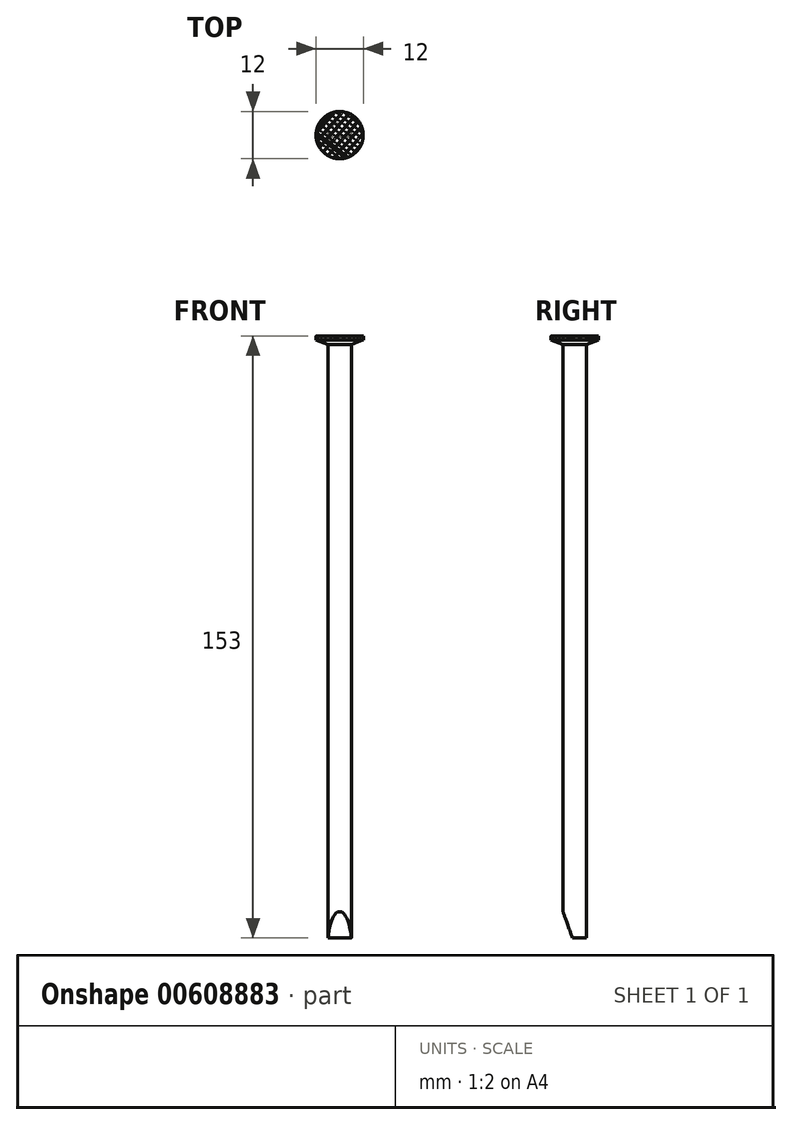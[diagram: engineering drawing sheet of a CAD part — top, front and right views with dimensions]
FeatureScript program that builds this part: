
annotation { "Feature Type Name" : "Feature", "Feature Type Description" : "" }
export const myFeature = defineFeature(function(context is Context, id is Id, definition is map)
    precondition{}
    {
        {
            var Q0;
            Q0=qCreatedBy(makeId("Top.planeOp"),FACE);
            var sketch = newSketch(context, id + "F0", { "sketchPlane" : qUnion([Q0])});
            skCircle(sketch, "E0", {"center": v(0, 0) * mm, "radius": 3 * mm});
            skSolve(sketch);
        }
        {
            var Q0;
            Q0=makeQuery(id+"F0.imprint","IMPRINT",FACE,{"disambiguationData":[TD([[makeQuery(id+"F0.imprint","IMPRINT",EDGE,{"derivedFrom":sQuery(id+"F0.wireOp",EDGE,"E0")}),1.0]])]});
            extrude(context, id + "F1", {"entities" : qUnion([Q0]), "depth" : 150 * mm, "offsetDistance" : 25 * mm});
        }
        {
            var Q0;
            Q0=makeQuery(id+"F1.opExtrude","CAP_FACE",FACE,{"disambiguationData":[OSD([sQuery(id+"F0.wireOp",EDGE,"E0")])],"isStart":false});
            var sketch = newSketch(context, id + "F2", { "sketchPlane" : qUnion([Q0])});
            skCircle(sketch, "E1", {"center": v(0, 0) * mm, "radius": 6 * mm});
            skSolve(sketch);
        }
        {
            var Q0;
            Q0 = qSketchRegion(id + "F2", true);
            extrude(context, id + "F3", {"entities" : qUnion([Q0]), "operationType" : NewBodyOperationType.ADD, "depth" : 3 * mm, "offsetDistance" : 25 * mm});
        }
        {
            var Q0;
            Q0=makeQuery(id+"F3.opExtrude","CAP_EDGE",EDGE,{"disambiguationData":[OSD([sQuery(id+"F2.wireOp",EDGE,"E1")])],"isStart":true});
            chamfer(context, id + "F4", {"entities" : qUnion([Q0]), "chamferType" : ChamferType.TWO_OFFSETS, "width1" : 2 * mm, "oppositeDirection" : false, "width2" : 5 * mm, "tangentPropagation" : true});
        }
        {
            var Q0;
            Q0=makeQuery(id+"F3.opExtrude","CAP_FACE",FACE,{"disambiguationData":[OSD([sQuery(id+"F2.wireOp",EDGE,"E1")])],"isStart":false});
            var sketch = newSketch(context, id + "F5", { "sketchPlane" : qUnion([Q0])});
            skLineSegment(sketch, "E2", {"start": v(-21.1, 10.28) * mm, "end": v(9.5, -13.54) * mm});
            skLineSegment(sketch, "E3", {"start": v(9.5, -13.54) * mm, "end": v(9.07, -14.09) * mm});
            skLineSegment(sketch, "E4", {"start": v(9.07, -14.09) * mm, "end": v(-21.1, 9.4) * mm});
            skLineSegment(sketch, "E5", {"start": v(-21.1, 9.4) * mm, "end": v(-21.1, 10.28) * mm});
            skLineSegment(sketch, "E6.1.0.0", {"start": v(-19.1, 10.28) * mm, "end": v(11.5, -13.54) * mm});
            skLineSegment(sketch, "E6.1.0.1", {"start": v(11.07, -14.09) * mm, "end": v(-19.1, 9.4) * mm});
            skLineSegment(sketch, "E6.1.0.2", {"start": v(-19.1, 9.4) * mm, "end": v(-19.1, 10.28) * mm});
            skLineSegment(sketch, "E6.1.0.3", {"start": v(11.5, -13.54) * mm, "end": v(11.07, -14.09) * mm});
            skLineSegment(sketch, "E6.2.0.0", {"start": v(-17.1, 10.28) * mm, "end": v(13.5, -13.54) * mm});
            skLineSegment(sketch, "E6.2.0.1", {"start": v(13.07, -14.09) * mm, "end": v(-17.1, 9.4) * mm});
            skLineSegment(sketch, "E6.2.0.2", {"start": v(-17.1, 9.4) * mm, "end": v(-17.1, 10.28) * mm});
            skLineSegment(sketch, "E6.2.0.3", {"start": v(13.5, -13.54) * mm, "end": v(13.07, -14.09) * mm});
            skLineSegment(sketch, "E6.3.0.0", {"start": v(-15.1, 10.28) * mm, "end": v(15.5, -13.54) * mm});
            skLineSegment(sketch, "E6.3.0.1", {"start": v(15.07, -14.09) * mm, "end": v(-15.1, 9.4) * mm});
            skLineSegment(sketch, "E6.3.0.2", {"start": v(-15.1, 9.4) * mm, "end": v(-15.1, 10.28) * mm});
            skLineSegment(sketch, "E6.3.0.3", {"start": v(15.5, -13.54) * mm, "end": v(15.07, -14.09) * mm});
            skLineSegment(sketch, "E6.4.0.0", {"start": v(-13.1, 10.28) * mm, "end": v(17.5, -13.54) * mm});
            skLineSegment(sketch, "E6.4.0.1", {"start": v(17.07, -14.09) * mm, "end": v(-13.1, 9.4) * mm});
            skLineSegment(sketch, "E6.4.0.2", {"start": v(-13.1, 9.4) * mm, "end": v(-13.1, 10.28) * mm});
            skLineSegment(sketch, "E6.4.0.3", {"start": v(17.5, -13.54) * mm, "end": v(17.07, -14.09) * mm});
            skLineSegment(sketch, "E6.5.0.0", {"start": v(-11.1, 10.28) * mm, "end": v(19.5, -13.54) * mm});
            skLineSegment(sketch, "E6.5.0.1", {"start": v(19.07, -14.09) * mm, "end": v(-11.1, 9.4) * mm});
            skLineSegment(sketch, "E6.5.0.2", {"start": v(-11.1, 9.4) * mm, "end": v(-11.1, 10.28) * mm});
            skLineSegment(sketch, "E6.5.0.3", {"start": v(19.5, -13.54) * mm, "end": v(19.07, -14.09) * mm});
            skLineSegment(sketch, "E6.6.0.0", {"start": v(-9.1, 10.28) * mm, "end": v(21.5, -13.54) * mm});
            skLineSegment(sketch, "E6.6.0.1", {"start": v(21.07, -14.09) * mm, "end": v(-9.1, 9.4) * mm});
            skLineSegment(sketch, "E6.6.0.2", {"start": v(-9.1, 9.4) * mm, "end": v(-9.1, 10.28) * mm});
            skLineSegment(sketch, "E6.6.0.3", {"start": v(21.5, -13.54) * mm, "end": v(21.07, -14.09) * mm});
            skLineSegment(sketch, "E6.7.0.0", {"start": v(-7.1, 10.28) * mm, "end": v(23.5, -13.54) * mm});
            skLineSegment(sketch, "E6.7.0.1", {"start": v(23.07, -14.09) * mm, "end": v(-7.1, 9.4) * mm});
            skLineSegment(sketch, "E6.7.0.2", {"start": v(-7.1, 9.4) * mm, "end": v(-7.1, 10.28) * mm});
            skLineSegment(sketch, "E6.7.0.3", {"start": v(23.5, -13.54) * mm, "end": v(23.07, -14.09) * mm});
            skLineSegment(sketch, "E6.8.0.0", {"start": v(-5.1, 10.28) * mm, "end": v(25.5, -13.54) * mm});
            skLineSegment(sketch, "E6.8.0.1", {"start": v(25.07, -14.09) * mm, "end": v(-5.1, 9.4) * mm});
            skLineSegment(sketch, "E6.8.0.2", {"start": v(-5.1, 9.4) * mm, "end": v(-5.1, 10.28) * mm});
            skLineSegment(sketch, "E6.8.0.3", {"start": v(25.5, -13.54) * mm, "end": v(25.07, -14.09) * mm});
            skLineSegment(sketch, "E6.9.0.0", {"start": v(-3.1, 10.28) * mm, "end": v(27.5, -13.54) * mm});
            skLineSegment(sketch, "E6.9.0.1", {"start": v(27.07, -14.09) * mm, "end": v(-3.1, 9.4) * mm});
            skLineSegment(sketch, "E6.9.0.2", {"start": v(-3.1, 9.4) * mm, "end": v(-3.1, 10.28) * mm});
            skLineSegment(sketch, "E6.9.0.3", {"start": v(27.5, -13.54) * mm, "end": v(27.07, -14.09) * mm});
            skLineSegment(sketch, "E6.direction1", {"start": v(-21.1, 9.4) * mm, "end": v(-19.1, 9.4) * mm, "construction": true});
            skSolve(sketch);
        }
        {
            var Q0;
            {var subQ0=sQuery(id+"F5.wireOp",EDGE,"E5");Q0=makeQuery(id+"F5.imprint","IMPRINT",FACE,{"disambiguationData":[TD([[makeQuery(id+"F5.imprint","IMPRINT",EDGE,{"derivedFrom":subQ0}),-1.0]])]});}
            var Q1;
            {var subQ0=sQuery(id+"F5.wireOp",EDGE,"E6.9.0.1");var subQ1=makeQuery(id+"F3.opExtrude","CAP_EDGE",EDGE,{"disambiguationData":[OSD([sQuery(id+"F2.wireOp",EDGE,"E1")])],"isStart":false});var subQ2=makeQuery(id+"F5.imprint","INTERSECT",VERTEX,{"disambiguationData":[OD(0.0)],"derivedFrom":[subQ1,subQ0]});Q1=makeQuery(id+"F5.imprint","IMPRINT",FACE,{"disambiguationData":[TD([[makeQuery(id+"F5.imprint","IMPRINT",EDGE,{"disambiguationData":[TD([[subQ2,-1.0]])],"derivedFrom":subQ0}),-1.0]])]});}
            var Q2;
            {var subQ0=sQuery(id+"F5.wireOp",EDGE,"E6.8.0.0");var subQ1=makeQuery(id+"F3.opExtrude","CAP_EDGE",EDGE,{"disambiguationData":[OSD([sQuery(id+"F2.wireOp",EDGE,"E1")])],"isStart":false});var subQ2=makeQuery(id+"F5.imprint","INTERSECT",VERTEX,{"disambiguationData":[OD(0.0)],"derivedFrom":[subQ1,subQ0]});Q2=makeQuery(id+"F5.imprint","IMPRINT",FACE,{"disambiguationData":[TD([[makeQuery(id+"F5.imprint","IMPRINT",EDGE,{"disambiguationData":[TD([[subQ2,-1.0]])],"derivedFrom":subQ0}),-1.0]])]});}
            var Q3;
            {var subQ0=sQuery(id+"F5.wireOp",EDGE,"E6.7.0.0");var subQ1=makeQuery(id+"F3.opExtrude","CAP_EDGE",EDGE,{"disambiguationData":[OSD([sQuery(id+"F2.wireOp",EDGE,"E1")])],"isStart":false});var subQ2=makeQuery(id+"F5.imprint","INTERSECT",VERTEX,{"disambiguationData":[OD(0.0)],"derivedFrom":[subQ1,subQ0]});Q3=makeQuery(id+"F5.imprint","IMPRINT",FACE,{"disambiguationData":[TD([[makeQuery(id+"F5.imprint","IMPRINT",EDGE,{"disambiguationData":[TD([[subQ2,-1.0]])],"derivedFrom":subQ0}),-1.0]])]});}
            var Q4;
            {var subQ0=sQuery(id+"F5.wireOp",EDGE,"E6.6.0.0");var subQ1=makeQuery(id+"F3.opExtrude","CAP_EDGE",EDGE,{"disambiguationData":[OSD([sQuery(id+"F2.wireOp",EDGE,"E1")])],"isStart":false});var subQ2=makeQuery(id+"F5.imprint","INTERSECT",VERTEX,{"disambiguationData":[OD(0.0)],"derivedFrom":[subQ1,subQ0]});Q4=makeQuery(id+"F5.imprint","IMPRINT",FACE,{"disambiguationData":[TD([[makeQuery(id+"F5.imprint","IMPRINT",EDGE,{"disambiguationData":[TD([[subQ2,-1.0]])],"derivedFrom":subQ0}),-1.0]])]});}
            var Q5;
            {var subQ0=sQuery(id+"F5.wireOp",EDGE,"E6.5.0.0");var subQ1=makeQuery(id+"F3.opExtrude","CAP_EDGE",EDGE,{"disambiguationData":[OSD([sQuery(id+"F2.wireOp",EDGE,"E1")])],"isStart":false});var subQ2=makeQuery(id+"F5.imprint","INTERSECT",VERTEX,{"disambiguationData":[OD(0.0)],"derivedFrom":[subQ1,subQ0]});Q5=makeQuery(id+"F5.imprint","IMPRINT",FACE,{"disambiguationData":[TD([[makeQuery(id+"F5.imprint","IMPRINT",EDGE,{"disambiguationData":[TD([[subQ2,-1.0]])],"derivedFrom":subQ0}),-1.0]])]});}
            var Q6;
            {var subQ0=sQuery(id+"F5.wireOp",EDGE,"E6.4.0.0");var subQ1=makeQuery(id+"F3.opExtrude","CAP_EDGE",EDGE,{"disambiguationData":[OSD([sQuery(id+"F2.wireOp",EDGE,"E1")])],"isStart":false});var subQ2=makeQuery(id+"F5.imprint","INTERSECT",VERTEX,{"disambiguationData":[OD(0.0)],"derivedFrom":[subQ1,subQ0]});Q6=makeQuery(id+"F5.imprint","IMPRINT",FACE,{"disambiguationData":[TD([[makeQuery(id+"F5.imprint","IMPRINT",EDGE,{"disambiguationData":[TD([[subQ2,-1.0]])],"derivedFrom":subQ0}),-1.0]])]});}
            var Q7;
            {var subQ0=sQuery(id+"F5.wireOp",EDGE,"E6.3.0.0");var subQ1=makeQuery(id+"F3.opExtrude","CAP_EDGE",EDGE,{"disambiguationData":[OSD([sQuery(id+"F2.wireOp",EDGE,"E1")])],"isStart":false});var subQ2=makeQuery(id+"F5.imprint","INTERSECT",VERTEX,{"disambiguationData":[OD(0.0)],"derivedFrom":[subQ1,subQ0]});Q7=makeQuery(id+"F5.imprint","IMPRINT",FACE,{"disambiguationData":[TD([[makeQuery(id+"F5.imprint","IMPRINT",EDGE,{"disambiguationData":[TD([[subQ2,-1.0]])],"derivedFrom":subQ0}),-1.0]])]});}
            var Q8;
            {var subQ0=sQuery(id+"F5.wireOp",EDGE,"E6.2.0.0");var subQ1=makeQuery(id+"F3.opExtrude","CAP_EDGE",EDGE,{"disambiguationData":[OSD([sQuery(id+"F2.wireOp",EDGE,"E1")])],"isStart":false});var subQ2=makeQuery(id+"F5.imprint","INTERSECT",VERTEX,{"disambiguationData":[OD(0.0)],"derivedFrom":[subQ1,subQ0]});Q8=makeQuery(id+"F5.imprint","IMPRINT",FACE,{"disambiguationData":[TD([[makeQuery(id+"F5.imprint","IMPRINT",EDGE,{"disambiguationData":[TD([[subQ2,-1.0]])],"derivedFrom":subQ0}),-1.0]])]});}
            var Q9;
            {var subQ0=sQuery(id+"F5.wireOp",EDGE,"E6.1.0.0");var subQ1=makeQuery(id+"F3.opExtrude","CAP_EDGE",EDGE,{"disambiguationData":[OSD([sQuery(id+"F2.wireOp",EDGE,"E1")])],"isStart":false});var subQ2=makeQuery(id+"F5.imprint","INTERSECT",VERTEX,{"disambiguationData":[OD(0.0)],"derivedFrom":[subQ1,subQ0]});Q9=makeQuery(id+"F5.imprint","IMPRINT",FACE,{"disambiguationData":[TD([[makeQuery(id+"F5.imprint","IMPRINT",EDGE,{"disambiguationData":[TD([[subQ2,-1.0]])],"derivedFrom":subQ0}),-1.0]])]});}
            var Q10;
            {var subQ0=sQuery(id+"F5.wireOp",EDGE,"E2");var subQ1=makeQuery(id+"F3.opExtrude","CAP_EDGE",EDGE,{"disambiguationData":[OSD([sQuery(id+"F2.wireOp",EDGE,"E1")])],"isStart":false});var subQ2=makeQuery(id+"F5.imprint","INTERSECT",VERTEX,{"disambiguationData":[OD(0.0)],"derivedFrom":[subQ1,subQ0]});Q10=makeQuery(id+"F5.imprint","IMPRINT",FACE,{"disambiguationData":[TD([[makeQuery(id+"F5.imprint","IMPRINT",EDGE,{"disambiguationData":[TD([[subQ2,-1.0]])],"derivedFrom":subQ0}),-1.0]])]});}
            extrude(context, id + "F6", {"entities" : qUnion([Q0, Q1, Q2, Q3, Q4, Q5, Q6, Q7, Q8, Q9, Q10]), "operationType" : NewBodyOperationType.REMOVE, "oppositeDirection" : true, "depth" : 0.3 * mm, "offsetDistance" : 25 * mm});
        }
        {
            var Q0;
            {var subQ0=sQuery(id+"F2.wireOp",EDGE,"E1");Q0=makeQuery(id+"F6.boolean.opBoolean","SPLIT",FACE,{"disambiguationData":[TD([makeQuery(id+"F6.opExtrude","SWEPT_FACE",FACE,{"disambiguationData":[OSD([sQuery(id+"F5.wireOp",EDGE,"E6.1.0.0")])]})])],"derivedFrom":makeQuery(id+"F3.opExtrude","CAP_FACE",FACE,{"disambiguationData":[OSD([subQ0])],"isStart":false})});}
            var sketch = newSketch(context, id + "F7", { "sketchPlane" : qUnion([Q0])});
            skLineSegment(sketch, "E7", {"start": v(5.94, 12.42) * mm, "end": v(-14.13, -10.44) * mm});
            skLineSegment(sketch, "E8", {"start": v(-14.13, -10.44) * mm, "end": v(-14.64, -10) * mm});
            skLineSegment(sketch, "E9", {"start": v(-14.64, -10) * mm, "end": v(5.33, 12.76) * mm});
            skLineSegment(sketch, "E10", {"start": v(5.33, 12.76) * mm, "end": v(5.94, 12.42) * mm});
            skLineSegment(sketch, "E11.1.0.0", {"start": v(7.94, 12.42) * mm, "end": v(-12.13, -10.44) * mm});
            skLineSegment(sketch, "E11.1.0.1", {"start": v(-12.64, -10) * mm, "end": v(7.33, 12.76) * mm});
            skLineSegment(sketch, "E11.1.0.2", {"start": v(-12.13, -10.44) * mm, "end": v(-12.64, -10) * mm});
            skLineSegment(sketch, "E11.1.0.3", {"start": v(7.33, 12.76) * mm, "end": v(7.94, 12.42) * mm});
            skLineSegment(sketch, "E11.2.0.0", {"start": v(9.94, 12.42) * mm, "end": v(-10.13, -10.44) * mm});
            skLineSegment(sketch, "E11.2.0.1", {"start": v(-10.64, -10) * mm, "end": v(9.33, 12.76) * mm});
            skLineSegment(sketch, "E11.2.0.2", {"start": v(-10.13, -10.44) * mm, "end": v(-10.64, -10) * mm});
            skLineSegment(sketch, "E11.2.0.3", {"start": v(9.33, 12.76) * mm, "end": v(9.94, 12.42) * mm});
            skLineSegment(sketch, "E11.3.0.0", {"start": v(11.94, 12.42) * mm, "end": v(-8.13, -10.44) * mm});
            skLineSegment(sketch, "E11.3.0.1", {"start": v(-8.64, -10) * mm, "end": v(11.33, 12.76) * mm});
            skLineSegment(sketch, "E11.3.0.2", {"start": v(-8.13, -10.44) * mm, "end": v(-8.64, -10) * mm});
            skLineSegment(sketch, "E11.3.0.3", {"start": v(11.33, 12.76) * mm, "end": v(11.94, 12.42) * mm});
            skLineSegment(sketch, "E11.4.0.0", {"start": v(13.94, 12.42) * mm, "end": v(-6.13, -10.44) * mm});
            skLineSegment(sketch, "E11.4.0.1", {"start": v(-6.64, -10) * mm, "end": v(13.33, 12.76) * mm});
            skLineSegment(sketch, "E11.4.0.2", {"start": v(-6.13, -10.44) * mm, "end": v(-6.64, -10) * mm});
            skLineSegment(sketch, "E11.4.0.3", {"start": v(13.33, 12.76) * mm, "end": v(13.94, 12.42) * mm});
            skLineSegment(sketch, "E11.5.0.0", {"start": v(15.94, 12.42) * mm, "end": v(-4.13, -10.44) * mm});
            skLineSegment(sketch, "E11.5.0.1", {"start": v(-4.64, -10) * mm, "end": v(15.33, 12.76) * mm});
            skLineSegment(sketch, "E11.5.0.2", {"start": v(-4.13, -10.44) * mm, "end": v(-4.64, -10) * mm});
            skLineSegment(sketch, "E11.5.0.3", {"start": v(15.33, 12.76) * mm, "end": v(15.94, 12.42) * mm});
            skLineSegment(sketch, "E11.6.0.0", {"start": v(17.94, 12.42) * mm, "end": v(-2.13, -10.44) * mm});
            skLineSegment(sketch, "E11.6.0.1", {"start": v(-2.64, -10) * mm, "end": v(17.33, 12.76) * mm});
            skLineSegment(sketch, "E11.6.0.2", {"start": v(-2.13, -10.44) * mm, "end": v(-2.64, -10) * mm});
            skLineSegment(sketch, "E11.6.0.3", {"start": v(17.33, 12.76) * mm, "end": v(17.94, 12.42) * mm});
            skLineSegment(sketch, "E11.7.0.0", {"start": v(19.94, 12.42) * mm, "end": v(-0.13, -10.44) * mm});
            skLineSegment(sketch, "E11.7.0.1", {"start": v(-0.64, -10) * mm, "end": v(19.33, 12.76) * mm});
            skLineSegment(sketch, "E11.7.0.2", {"start": v(-0.13, -10.44) * mm, "end": v(-0.64, -10) * mm});
            skLineSegment(sketch, "E11.7.0.3", {"start": v(19.33, 12.76) * mm, "end": v(19.94, 12.42) * mm});
            skLineSegment(sketch, "E11.8.0.0", {"start": v(21.94, 12.42) * mm, "end": v(1.87, -10.44) * mm});
            skLineSegment(sketch, "E11.8.0.1", {"start": v(1.36, -10) * mm, "end": v(21.33, 12.76) * mm});
            skLineSegment(sketch, "E11.8.0.2", {"start": v(1.87, -10.44) * mm, "end": v(1.36, -10) * mm});
            skLineSegment(sketch, "E11.8.0.3", {"start": v(21.33, 12.76) * mm, "end": v(21.94, 12.42) * mm});
            skLineSegment(sketch, "E11.9.0.0", {"start": v(23.94, 12.42) * mm, "end": v(3.87, -10.44) * mm});
            skLineSegment(sketch, "E11.9.0.1", {"start": v(3.36, -10) * mm, "end": v(23.33, 12.76) * mm});
            skLineSegment(sketch, "E11.9.0.2", {"start": v(3.87, -10.44) * mm, "end": v(3.36, -10) * mm});
            skLineSegment(sketch, "E11.9.0.3", {"start": v(23.33, 12.76) * mm, "end": v(23.94, 12.42) * mm});
            skLineSegment(sketch, "E11.direction1", {"start": v(-14.64, -10) * mm, "end": v(-12.64, -10) * mm, "construction": true});
            skSolve(sketch);
        }
        {
            var Q0;
            {var subQ0=sQuery(id+"F7.wireOp",EDGE,"E10");Q0=makeQuery(id+"F7.imprint","IMPRINT",FACE,{"disambiguationData":[TD([[makeQuery(id+"F7.imprint","IMPRINT",EDGE,{"derivedFrom":subQ0}),-1.0]])]});}
            var Q1;
            {var subQ0=sQuery(id+"F7.wireOp",EDGE,"E11.1.0.3");Q1=makeQuery(id+"F7.imprint","IMPRINT",FACE,{"disambiguationData":[TD([[makeQuery(id+"F7.imprint","IMPRINT",EDGE,{"derivedFrom":subQ0}),-1.0]])]});}
            var Q2;
            {var subQ0=sQuery(id+"F7.wireOp",EDGE,"E11.2.0.3");Q2=makeQuery(id+"F7.imprint","IMPRINT",FACE,{"disambiguationData":[TD([[makeQuery(id+"F7.imprint","IMPRINT",EDGE,{"derivedFrom":subQ0}),-1.0]])]});}
            var Q3;
            {var subQ0=sQuery(id+"F7.wireOp",EDGE,"E11.3.0.3");Q3=makeQuery(id+"F7.imprint","IMPRINT",FACE,{"disambiguationData":[TD([[makeQuery(id+"F7.imprint","IMPRINT",EDGE,{"derivedFrom":subQ0}),-1.0]])]});}
            var Q4;
            {var subQ0=sQuery(id+"F7.wireOp",EDGE,"E11.4.0.3");Q4=makeQuery(id+"F7.imprint","IMPRINT",FACE,{"disambiguationData":[TD([[makeQuery(id+"F7.imprint","IMPRINT",EDGE,{"derivedFrom":subQ0}),-1.0]])]});}
            var Q5;
            {var subQ0=sQuery(id+"F7.wireOp",EDGE,"E11.5.0.3");Q5=makeQuery(id+"F7.imprint","IMPRINT",FACE,{"disambiguationData":[TD([[makeQuery(id+"F7.imprint","IMPRINT",EDGE,{"derivedFrom":subQ0}),-1.0]])]});}
            var Q6;
            {var subQ0=sQuery(id+"F7.wireOp",EDGE,"E11.6.0.3");Q6=makeQuery(id+"F7.imprint","IMPRINT",FACE,{"disambiguationData":[TD([[makeQuery(id+"F7.imprint","IMPRINT",EDGE,{"derivedFrom":subQ0}),-1.0]])]});}
            var Q7;
            Q7=makeQuery(id+"F7.imprint","IMPRINT",FACE,{"disambiguationData":[TD([[makeQuery(id+"F7.imprint","IMPRINT",EDGE,{"derivedFrom":sQuery(id+"F7.wireOp",EDGE,"E11.7.0.0")}),-1.0]])]});
            var Q8;
            Q8=makeQuery(id+"F7.imprint","IMPRINT",FACE,{"disambiguationData":[TD([[makeQuery(id+"F7.imprint","IMPRINT",EDGE,{"derivedFrom":sQuery(id+"F7.wireOp",EDGE,"E11.8.0.0")}),-1.0]])]});
            var Q9;
            {var subQ0=sQuery(id+"F7.wireOp",EDGE,"E11.6.0.2");Q9=makeQuery(id+"F7.imprint","IMPRINT",FACE,{"disambiguationData":[TD([[makeQuery(id+"F7.imprint","IMPRINT",EDGE,{"derivedFrom":subQ0}),-1.0]])]});}
            var Q10;
            {var subQ0=sQuery(id+"F7.wireOp",EDGE,"E11.4.0.2");Q10=makeQuery(id+"F7.imprint","IMPRINT",FACE,{"disambiguationData":[TD([[makeQuery(id+"F7.imprint","IMPRINT",EDGE,{"derivedFrom":subQ0}),-1.0]])]});}
            var Q11;
            {var subQ0=sQuery(id+"F7.wireOp",EDGE,"E11.3.0.2");Q11=makeQuery(id+"F7.imprint","IMPRINT",FACE,{"disambiguationData":[TD([[makeQuery(id+"F7.imprint","IMPRINT",EDGE,{"derivedFrom":subQ0}),-1.0]])]});}
            var Q12;
            {var subQ0=sQuery(id+"F7.wireOp",EDGE,"E11.2.0.2");Q12=makeQuery(id+"F7.imprint","IMPRINT",FACE,{"disambiguationData":[TD([[makeQuery(id+"F7.imprint","IMPRINT",EDGE,{"derivedFrom":subQ0}),-1.0]])]});}
            var Q13;
            {var subQ0=sQuery(id+"F7.wireOp",EDGE,"E11.1.0.2");Q13=makeQuery(id+"F7.imprint","IMPRINT",FACE,{"disambiguationData":[TD([[makeQuery(id+"F7.imprint","IMPRINT",EDGE,{"derivedFrom":subQ0}),-1.0]])]});}
            var Q14;
            {var subQ0=sQuery(id+"F7.wireOp",EDGE,"E8");Q14=makeQuery(id+"F7.imprint","IMPRINT",FACE,{"disambiguationData":[TD([[makeQuery(id+"F7.imprint","IMPRINT",EDGE,{"derivedFrom":subQ0}),-1.0]])]});}
            var Q15;
            {var subQ0=sQuery(id+"F7.wireOp",EDGE,"E11.5.0.2");Q15=makeQuery(id+"F7.imprint","IMPRINT",FACE,{"disambiguationData":[TD([[makeQuery(id+"F7.imprint","IMPRINT",EDGE,{"derivedFrom":subQ0}),-1.0]])]});}
            extrude(context, id + "F8", {"entities" : qUnion([Q0, Q1, Q2, Q3, Q4, Q5, Q6, Q7, Q8, Q9, Q10, Q11, Q12, Q13, Q14, Q15]), "operationType" : NewBodyOperationType.REMOVE, "oppositeDirection" : true, "depth" : 0.3 * mm, "offsetDistance" : 25 * mm});
        }
        {
            var Q0;
            Q0=qCreatedBy(makeId("Right.planeOp"),FACE);
            var sketch = newSketch(context, id + "F9", { "sketchPlane" : qUnion([Q0])});
            skLineSegment(sketch, "E12", {"start": v(-0.39, -0.47) * mm, "end": v(-4.5, 10.93) * mm});
            skLineSegment(sketch, "E13", {"start": v(-4.5, 10.93) * mm, "end": v(-6.4, -2.66) * mm});
            skLineSegment(sketch, "E14", {"start": v(-6.4, -2.66) * mm, "end": v(-0.39, -0.47) * mm});
            skSolve(sketch);
        }
        {
            var Q0;
            Q0=makeQuery(id+"F9.imprint","IMPRINT",FACE,{"disambiguationData":[TD([[makeQuery(id+"F9.imprint","IMPRINT",EDGE,{"derivedFrom":sQuery(id+"F9.wireOp",EDGE,"E12")}),1.0]])]});
            extrude(context, id + "F10", {"entities" : qUnion([Q0]), "operationType" : NewBodyOperationType.REMOVE, "oppositeDirection" : true, "depth" : 25 * mm, "offsetDistance" : 25 * mm, "hasSecondDirection" : true, "secondDirectionOppositeDirection" : false, "secondDirectionDepth" : 25 * mm});
        }
    });
